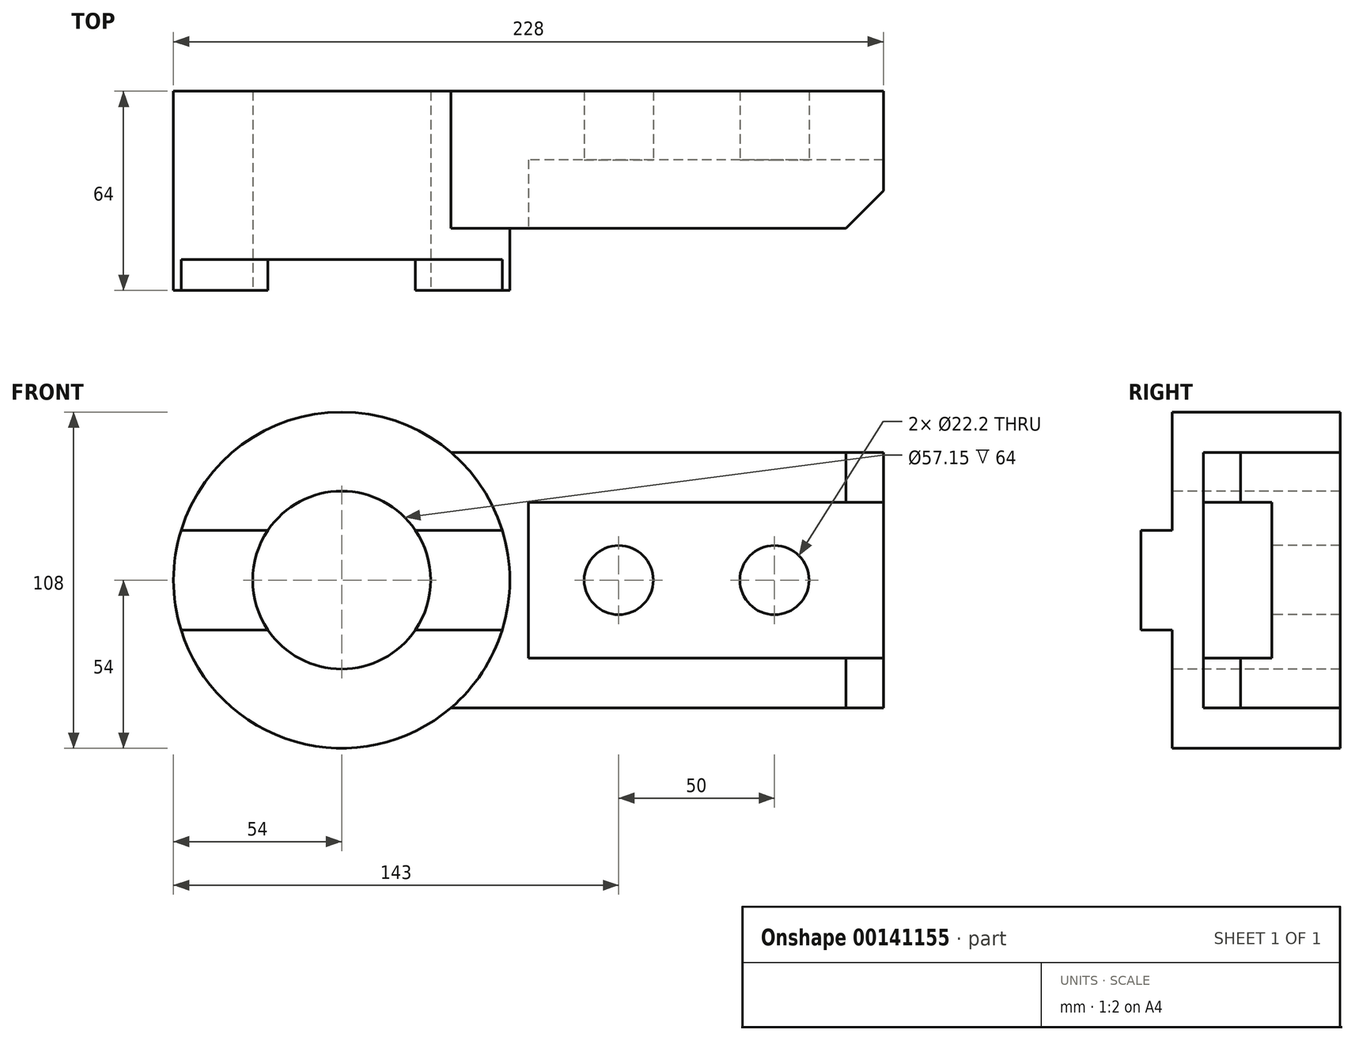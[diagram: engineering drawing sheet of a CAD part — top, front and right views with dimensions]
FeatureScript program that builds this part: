
annotation { "Feature Type Name" : "Feature", "Feature Type Description" : "" }
export const myFeature = defineFeature(function(context is Context, id is Id, definition is map)
    precondition{}
    {
        {
            var Q0;
            Q0=qCreatedBy(makeId("Right.planeOp"),FACE);
            cPlane(context, id + "F0", {"entities" : qUnion([Q0]), "cplaneType" : CPlaneType.OFFSET, "offset" : 60 * mm, "width" : 150 * mm, "height" : 150 * mm});
        }
        {
            var Q0;
            Q0=qCreatedBy(id+"F0.planeOp",FACE);
            var sketch = newSketch(context, id + "F1", { "sketchPlane" : qUnion([Q0])});
            skLineSegment(sketch, "E0", {"start": v(0, 25) * mm, "end": v(0, 41) * mm});
            skLineSegment(sketch, "E1", {"start": v(0, 41) * mm, "end": v(44, 41) * mm});
            skLineSegment(sketch, "E2", {"start": v(44, 41) * mm, "end": v(44, -41) * mm});
            skLineSegment(sketch, "E3", {"start": v(44, -41) * mm, "end": v(0, -41) * mm});
            skLineSegment(sketch, "E4", {"start": v(0, -41) * mm, "end": v(0, -25) * mm});
            skLineSegment(sketch, "E5", {"start": v(0, -25) * mm, "end": v(22, -25) * mm});
            skLineSegment(sketch, "E6", {"start": v(22, -25) * mm, "end": v(22, 25) * mm});
            skLineSegment(sketch, "E7", {"start": v(22, 25) * mm, "end": v(0, 25) * mm});
            skSolve(sketch);
        }
        {
            var Q0;
            Q0=makeQuery(id+"F1.imprint","IMPRINT",FACE,{"disambiguationData":[TD([[makeQuery(id+"F1.imprint","IMPRINT",EDGE,{"derivedFrom":sQuery(id+"F1.wireOp",EDGE,"E0")}),-1.0]])]});
            extrude(context, id + "F2", {"entities" : qUnion([Q0]), "depth" : 114 * mm});
        }
        {
            var Q0;
            Q0=makeQuery(id+"F2.opExtrude","SWEPT_FACE",FACE,{"disambiguationData":[OSD([sQuery(id+"F1.wireOp",EDGE,"E1")])]});
            var sketch = newSketch(context, id + "F3", { "sketchPlane" : qUnion([Q0])});
            skLineSegment(sketch, "E8.0", {"start": v(174, 0) * mm, "end": v(60, 0) * mm});
            skLineSegment(sketch, "E8.1", {"start": v(174, 0) * mm, "end": v(174, 44) * mm});
            skLineSegment(sketch, "E9", {"start": v(162, 0) * mm, "end": v(174, 12) * mm});
            skSolve(sketch);
        }
        {
            var Q0;
            Q0 = qSketchRegion(id + "F3", true);
            extrude(context, id + "F4", {"entities" : qUnion([Q0]), "operationType" : NewBodyOperationType.REMOVE, "endBound" : BoundingType.THROUGH_ALL, "oppositeDirection" : true, "depth" : 25 * mm});
        }
        {
            var Q0;
            Q0=makeQuery(id+"F2.opExtrude","SWEPT_FACE",FACE,{"disambiguationData":[OSD([sQuery(id+"F1.wireOp",EDGE,"E6")])]});
            var sketch = newSketch(context, id + "F5", { "sketchPlane" : qUnion([Q0])});
            skCircle(sketch, "E10", {"center": v(89, 0) * mm, "radius": 11.1 * mm});
            skCircle(sketch, "E11", {"center": v(139, 0) * mm, "radius": 11.1 * mm});
            skSolve(sketch);
        }
        {
            var Q0;
            Q0 = qSketchRegion(id + "F5", true);
            extrude(context, id + "F6", {"entities" : qUnion([Q0]), "operationType" : NewBodyOperationType.REMOVE, "endBound" : BoundingType.THROUGH_ALL, "oppositeDirection" : true, "depth" : 25 * mm});
        }
        {
            var Q0;
            Q0=qCreatedBy(makeId("Front.planeOp"),FACE);
            var sketch = newSketch(context, id + "F7", { "sketchPlane" : qUnion([Q0])});
            skCircle(sketch, "E12", {"center": v(0, 0) * mm, "radius": 28.58 * mm});
            skCircle(sketch, "E13", {"center": v(0, 0) * mm, "radius": 54 * mm});
            skSolve(sketch);
        }
        {
            var Q0;
            Q0=makeQuery(id+"F7.imprint","IMPRINT",FACE,{"disambiguationData":[TD([[makeQuery(id+"F7.imprint","IMPRINT",EDGE,{"derivedFrom":sQuery(id+"F7.wireOp",EDGE,"E12")}),-1.0]])]});
            var Q1;
            Q1=makeQuery(id+"F2.opExtrude","SWEPT_FACE",FACE,{"disambiguationData":[OSD([sQuery(id+"F1.wireOp",EDGE,"E2")])]});
            extrude(context, id + "F8", {"entities" : qUnion([Q0]), "operationType" : NewBodyOperationType.ADD, "endBound" : BoundingType.UP_TO_SURFACE, "oppositeDirection" : true, "endBoundEntityFace" : qUnion([Q1]), "depth" : 25 * mm, "hasSecondDirection" : true, "secondDirectionOppositeDirection" : false, "secondDirectionDepth" : 10 * mm});
        }
        {
            var Q0;
            Q0=makeQuery(id+"F8.opExtrude","CAP_FACE",FACE,{"disambiguationData":[OSD([sQuery(id+"F7.wireOp",EDGE,"E12"),sQuery(id+"F7.wireOp",EDGE,"E13")])],"isStart":true});
            var sketch = newSketch(context, id + "F9", { "sketchPlane" : qUnion([Q0])});
            skLineSegment(sketch, "E14", {"start": v(-51.58, 16) * mm, "end": v(-23.68, 16) * mm});
            skLineSegment(sketch, "E15", {"start": v(-51.58, -16) * mm, "end": v(-23.68, -16) * mm});
            skLineSegment(sketch, "E16", {"start": v(23.68, 16) * mm, "end": v(51.58, 16) * mm});
            skLineSegment(sketch, "E17", {"start": v(23.68, -16) * mm, "end": v(51.58, -16) * mm});
            skCircle(sketch, "E18.0", {"center": v(0, 0) * mm, "radius": 54 * mm});
            skCircle(sketch, "E18.1", {"center": v(0, 0) * mm, "radius": 28.58 * mm});
            skSolve(sketch);
        }
        {
            var Q0;
            {var subQ0=sQuery(id+"F9.wireOp",EDGE,"E14");Q0=makeQuery(id+"F9.imprint","IMPRINT",FACE,{"disambiguationData":[TD([[makeQuery(id+"F9.imprint","IMPRINT",EDGE,{"derivedFrom":subQ0}),-1.0]])]});}
            var Q1;
            {var subQ0=sQuery(id+"F9.wireOp",EDGE,"E16");Q1=makeQuery(id+"F9.imprint","IMPRINT",FACE,{"disambiguationData":[TD([[makeQuery(id+"F9.imprint","IMPRINT",EDGE,{"derivedFrom":subQ0}),-1.0]])]});}
            extrude(context, id + "F10", {"entities" : qUnion([Q0, Q1]), "operationType" : NewBodyOperationType.ADD, "depth" : 10 * mm});
        }
        {
            var Q0;
            Q0=makeQuery(id+"F2.opExtrude","CAP_FACE",FACE,{"disambiguationData":[OSD([sQuery(id+"F1.wireOp",EDGE,"E0"),sQuery(id+"F1.wireOp",EDGE,"E1"),sQuery(id+"F1.wireOp",EDGE,"E2"),sQuery(id+"F1.wireOp",EDGE,"E3"),sQuery(id+"F1.wireOp",EDGE,"E4"),sQuery(id+"F1.wireOp",EDGE,"E5"),sQuery(id+"F1.wireOp",EDGE,"E6"),sQuery(id+"F1.wireOp",EDGE,"E7")])],"isStart":true});
            var sketch = newSketch(context, id + "F11", { "sketchPlane" : qUnion([Q0])});
            skLineSegment(sketch, "E19.0", {"start": v(-44, 41) * mm, "end": v(-44, -41) * mm});
            skLineSegment(sketch, "E19.1", {"start": v(0, 41) * mm, "end": v(-44, 41) * mm});
            skLineSegment(sketch, "E20", {"start": v(0, 41) * mm, "end": v(0, -41) * mm});
            skLineSegment(sketch, "E21", {"start": v(0, -41) * mm, "end": v(-44, -41) * mm});
            skSolve(sketch);
        }
        {
            var Q0;
            Q0 = qSketchRegion(id + "F11", true);
            extrude(context, id + "F12", {"entities" : qUnion([Q0]), "operationType" : NewBodyOperationType.ADD, "endBound" : BoundingType.UP_TO_NEXT, "depth" : 25 * mm});
        }
    });
